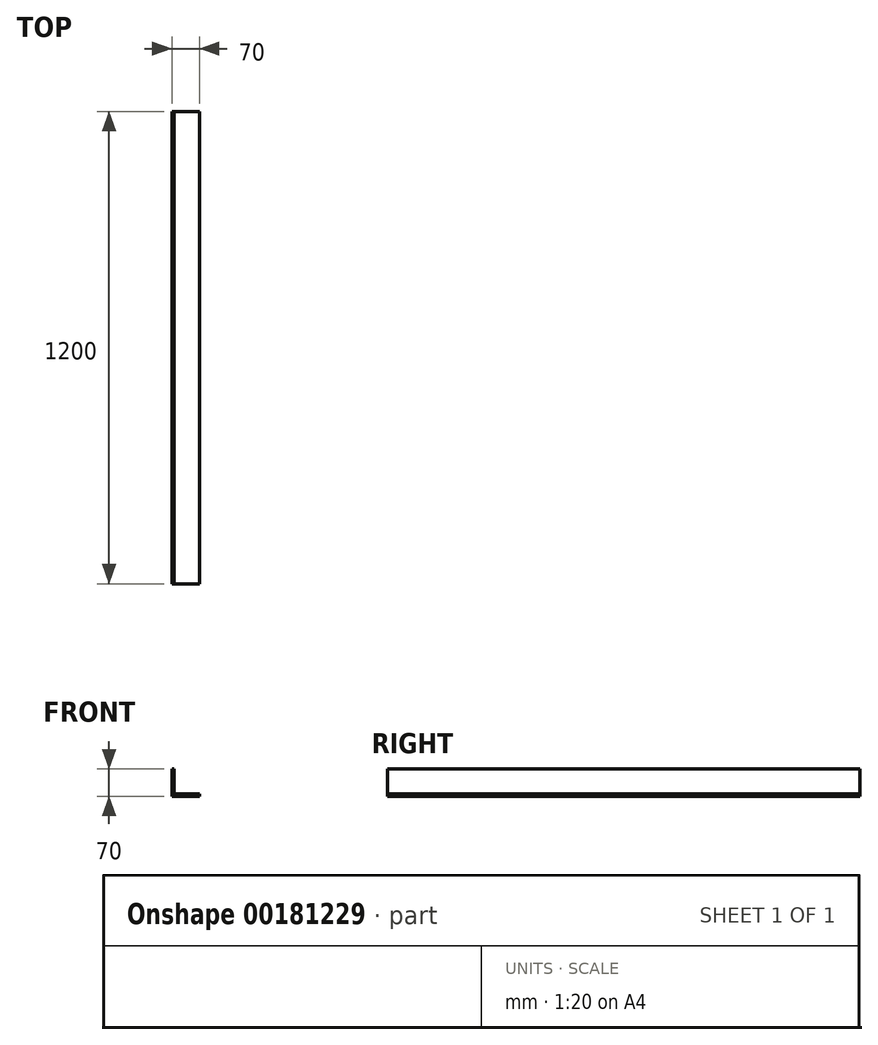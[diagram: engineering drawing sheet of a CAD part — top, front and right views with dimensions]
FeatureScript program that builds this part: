
annotation { "Feature Type Name" : "Feature", "Feature Type Description" : "" }
export const myFeature = defineFeature(function(context is Context, id is Id, definition is map)
    precondition{}
    {
        {
            var Q0;
            Q0=qCreatedBy(makeId("Front.planeOp"),FACE);
            var sketch = newSketch(context, id + "F0", { "sketchPlane" : qUnion([Q0])});
            skLineSegment(sketch, "E0", {"start": v(0, 0) * mm, "end": v(0, 70) * mm});
            skLineSegment(sketch, "E1", {"start": v(0, 0) * mm, "end": v(70, 0) * mm});
            skLineSegment(sketch, "E2.0", {"start": v(6, 6) * mm, "end": v(6, 70) * mm});
            skLineSegment(sketch, "E2.1", {"start": v(6, 6) * mm, "end": v(70, 6) * mm});
            skLineSegment(sketch, "E3", {"start": v(0, 70) * mm, "end": v(6, 70) * mm});
            skLineSegment(sketch, "E4", {"start": v(70, 6) * mm, "end": v(70, 0) * mm});
            skSolve(sketch);
        }
        {
            var Q0;
            Q0=makeQuery(id+"F0.imprint","IMPRINT",FACE,{"disambiguationData":[TD([[makeQuery(id+"F0.imprint","IMPRINT",EDGE,{"derivedFrom":sQuery(id+"F0.wireOp",EDGE,"E0")}),-1.0]])]});
            extrude(context, id + "F1", {"entities" : qUnion([Q0]), "depth" : 1200 * mm});
        }
    });
